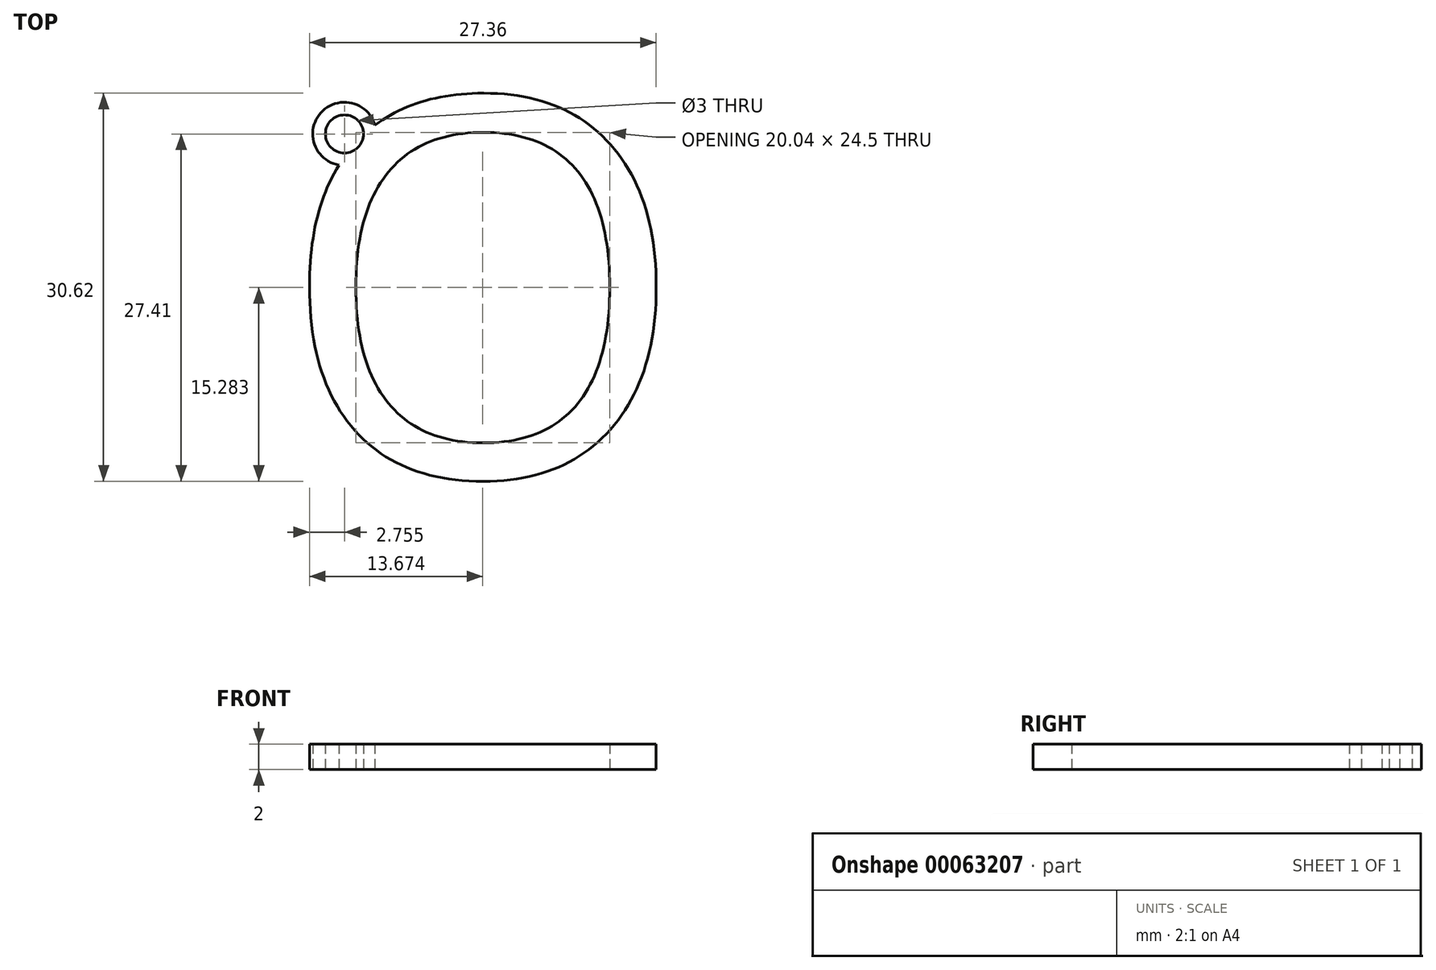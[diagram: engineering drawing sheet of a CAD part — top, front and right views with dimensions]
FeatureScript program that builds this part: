
annotation { "Feature Type Name" : "Feature", "Feature Type Description" : "" }
export const myFeature = defineFeature(function(context is Context, id is Id, definition is map)
    precondition{}
    {
        {
            var Q0;
            Q0=qCreatedBy(makeId("Top.planeOp"),FACE);
            var sketch = newSketch(context, id + "F0", { "sketchPlane" : qUnion([Q0])});
            skText(sketch, "E0", { "text": "O", "fontName": "OpenSans-Regular.ttf"});
            skCircle(sketch, "E1", {"center": v(-27.3, 27) * mm, "radius": 2.5 * mm});
            skCircle(sketch, "E2", {"center": v(-27.3, 27) * mm, "radius": 1.5 * mm});
            const initialGuessF0  = {"E0": [-0.03261, 0, 1, 0, 0.03]};
            skSetInitialGuess(sketch, initialGuessF0);
            skSolve(sketch);
        }
        {
            var Q0;
            Q0=makeQuery(id+"F0.imprint","IMPRINT",FACE,{"disambiguationData":[TD([[makeQuery(id+"F0.imprint","IMPRINT",EDGE,{"derivedFrom":sQuery(id+"F0.wireOp",EDGE,"E0.sketch_text.stroke-0")}),-1.0]])]});
            var Q1;
            {var subQ0=sQuery(id+"F0.wireOp",EDGE,"E1");var subQ1=sQuery(id+"F0.wireOp",EDGE,"E0.sketch_text.stroke-4");var subQ2=makeQuery(id+"F0.imprint","INTERSECT",VERTEX,{"derivedFrom":[subQ1,subQ0]});Q1=makeQuery(id+"F0.imprint","IMPRINT",FACE,{"disambiguationData":[TD([[makeQuery(id+"F0.imprint","IMPRINT",EDGE,{"disambiguationData":[TD([[subQ2,-1.0]])],"derivedFrom":subQ1}),1.0]])]});}
            var Q2;
            {var subQ0=sQuery(id+"F0.wireOp",EDGE,"E1");var subQ1=sQuery(id+"F0.wireOp",EDGE,"E0.sketch_text.stroke-4");var subQ2=makeQuery(id+"F0.imprint","INTERSECT",VERTEX,{"derivedFrom":[subQ1,subQ0]});Q2=makeQuery(id+"F0.imprint","IMPRINT",FACE,{"disambiguationData":[TD([[makeQuery(id+"F0.imprint","IMPRINT",EDGE,{"disambiguationData":[TD([[subQ2,-1.0]])],"derivedFrom":subQ1}),-1.0]])]});}
            extrude(context, id + "F1", {"entities" : qUnion([Q0, Q1, Q2]), "depth" : 2 * mm});
        }
    });
